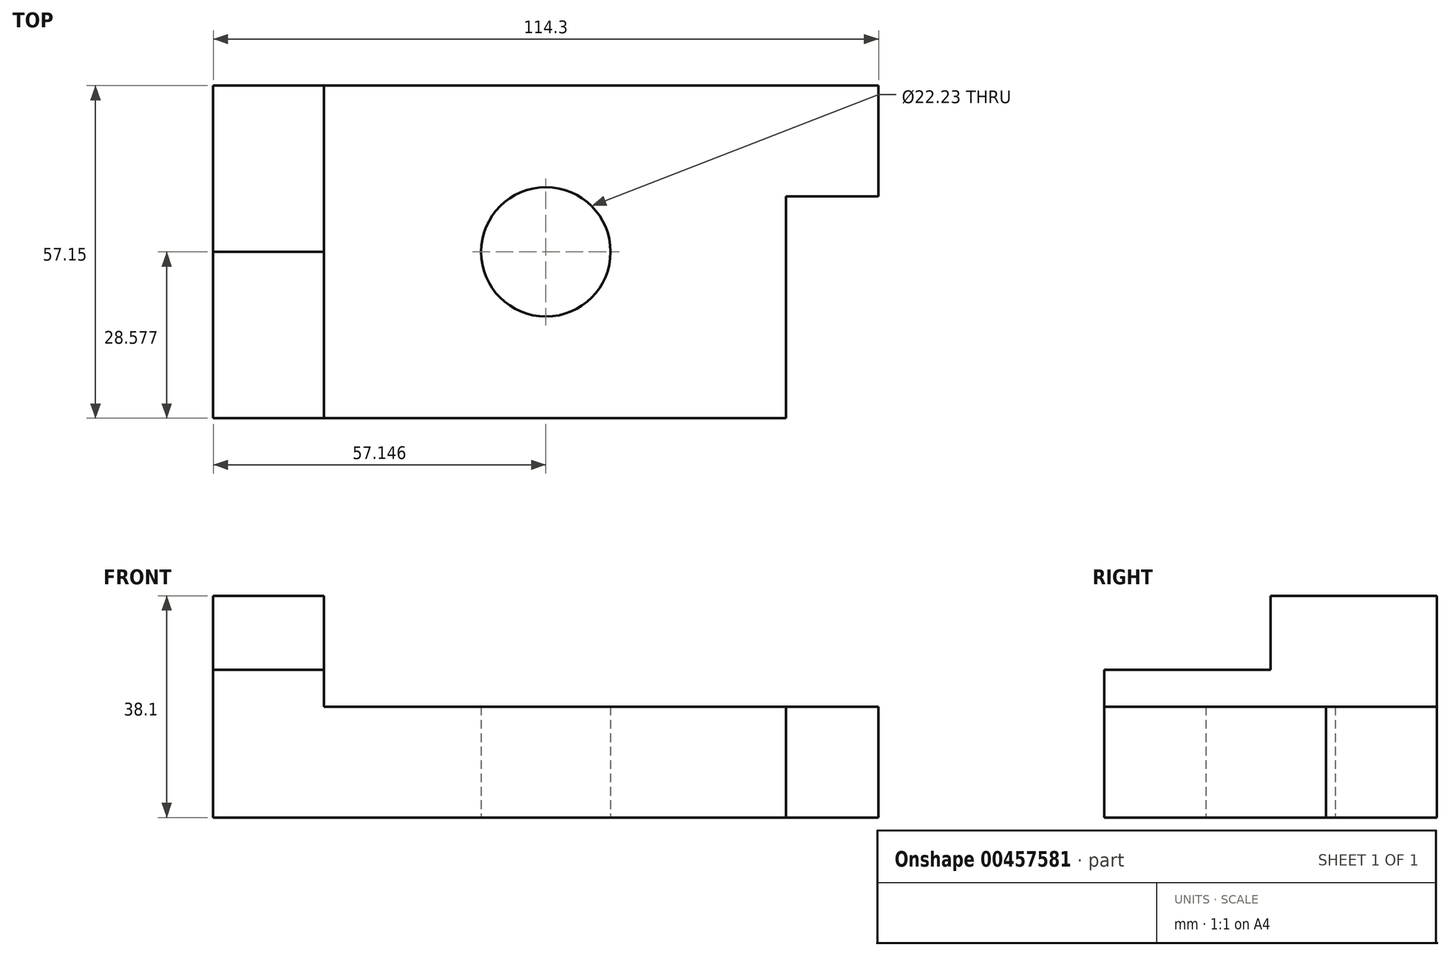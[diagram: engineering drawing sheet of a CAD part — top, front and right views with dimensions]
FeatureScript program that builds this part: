
annotation { "Feature Type Name" : "Feature", "Feature Type Description" : "" }
export const myFeature = defineFeature(function(context is Context, id is Id, definition is map)
    precondition{}
    {
        {
            var Q0;
            Q0=qCreatedBy(makeId("Top.planeOp"),FACE);
            var sketch = newSketch(context, id + "F0", { "sketchPlane" : qUnion([Q0])});
            skLineSegment(sketch, "E0.bottom", {"start": v(-57.46, 22.92) * mm, "end": v(56.84, 22.92) * mm});
            skLineSegment(sketch, "E0.top", {"start": v(-57.46, -34.23) * mm, "end": v(40.96, -34.23) * mm});
            skLineSegment(sketch, "E0.left", {"start": v(-57.46, 22.92) * mm, "end": v(-57.46, -34.23) * mm});
            skLineSegment(sketch, "E0.right", {"start": v(56.84, 22.92) * mm, "end": v(56.84, 3.87) * mm});
            skLineSegment(sketch, "E1.top", {"start": v(56.84, 3.87) * mm, "end": v(40.96, 3.87) * mm});
            skLineSegment(sketch, "E1.right", {"start": v(40.96, -34.23) * mm, "end": v(40.96, 3.87) * mm});
            skLineSegment(sketch, "E2.bottom", {"start": v(-57.46, 22.92) * mm, "end": v(-38.41, 22.92) * mm});
            skLineSegment(sketch, "E2.top", {"start": v(-57.46, -34.23) * mm, "end": v(-38.41, -34.23) * mm});
            skLineSegment(sketch, "E2.right", {"start": v(-38.41, 22.92) * mm, "end": v(-38.41, -34.23) * mm});
            skLineSegment(sketch, "E3.top", {"start": v(-57.46, -5.65) * mm, "end": v(-38.41, -5.65) * mm});
            skLineSegment(sketch, "E3.left", {"start": v(-57.46, 22.92) * mm, "end": v(-57.46, -5.65) * mm});
            skLineSegment(sketch, "E3.right", {"start": v(-38.41, 22.92) * mm, "end": v(-38.41, -5.65) * mm});
            skLineSegment(sketch, "E4.bottom", {"start": v(56.84, 22.92) * mm, "end": v(-0.31, 22.92) * mm});
            skCircle(sketch, "E5", {"center": v(-0.31, -5.65) * mm, "radius": 11.11 * mm});
            skSolve(sketch);
        }
        {
            var Q0;
            Q0=qSketchRegion(id+"F0",true);
            extrude(context, id + "F1", {"entities" : qUnion([Q0]), "depth" : 19.05 * mm});
        }
        {
            var Q0;
            Q0=makeQuery(id+"F1.opExtrude","CAP_FACE",FACE,{"disambiguationData":[OSD([sQuery(id+"F0.wireOp",EDGE,"E0.bottom"),sQuery(id+"F0.wireOp",EDGE,"E0.top"),sQuery(id+"F0.wireOp",EDGE,"E1.top"),sQuery(id+"F0.wireOp",EDGE,"E1.right"),sQuery(id+"F0.wireOp",EDGE,"E2.top"),sQuery(id+"F0.wireOp",EDGE,"E0.left"),sQuery(id+"F0.wireOp",EDGE,"E2.bottom"),sQuery(id+"F0.wireOp",EDGE,"E3.left"),sQuery(id+"F0.wireOp",EDGE,"E4.bottom"),sQuery(id+"F0.wireOp",EDGE,"E0.right"),sQuery(id+"F0.wireOp",EDGE,"E5")])],"isStart":false});
            var sketch = newSketch(context, id + "F2", { "sketchPlane" : qUnion([Q0])});
            skLineSegment(sketch, "E6.bottom", {"start": v(-57.46, 22.92) * mm, "end": v(-38.41, 22.92) * mm});
            skLineSegment(sketch, "E6.top", {"start": v(-57.46, -34.23) * mm, "end": v(-38.41, -34.23) * mm});
            skLineSegment(sketch, "E6.left", {"start": v(-57.46, 22.92) * mm, "end": v(-57.46, -34.23) * mm});
            skLineSegment(sketch, "E6.right", {"start": v(-38.41, 22.92) * mm, "end": v(-38.41, -34.23) * mm});
            skSolve(sketch);
        }
        {
            var Q0;
            Q0=makeQuery(id+"F2.imprint","IMPRINT",FACE,{"disambiguationData":[TD([[makeQuery(id+"F2.imprint","IMPRINT",EDGE,{"derivedFrom":sQuery(id+"F2.wireOp",EDGE,"E6.bottom")}),-1.0]])]});
            extrude(context, id + "F3", {"entities" : qUnion([Q0]), "operationType" : NewBodyOperationType.ADD, "depth" : 6.35 * mm});
        }
        {
            var Q0;
            Q0=makeQuery(id+"F3.opExtrude","CAP_FACE",FACE,{"disambiguationData":[OSD([sQuery(id+"F2.wireOp",EDGE,"E6.bottom"),sQuery(id+"F2.wireOp",EDGE,"E6.top"),sQuery(id+"F2.wireOp",EDGE,"E6.left"),sQuery(id+"F2.wireOp",EDGE,"E6.right")])],"isStart":false});
            var sketch = newSketch(context, id + "F4", { "sketchPlane" : qUnion([Q0])});
            skLineSegment(sketch, "E7.bottom", {"start": v(-57.46, 22.92) * mm, "end": v(-38.41, 22.92) * mm});
            skLineSegment(sketch, "E7.top", {"start": v(-57.46, -5.65) * mm, "end": v(-38.41, -5.65) * mm});
            skLineSegment(sketch, "E7.left", {"start": v(-57.46, 22.92) * mm, "end": v(-57.46, -5.65) * mm});
            skLineSegment(sketch, "E7.right", {"start": v(-38.41, 22.92) * mm, "end": v(-38.41, -5.65) * mm});
            skSolve(sketch);
        }
        {
            var Q0;
            Q0=qSketchRegion(id+"F4",true);
            extrude(context, id + "F5", {"entities" : qUnion([Q0]), "operationType" : NewBodyOperationType.ADD, "depth" : 12.7 * mm});
        }
    });
